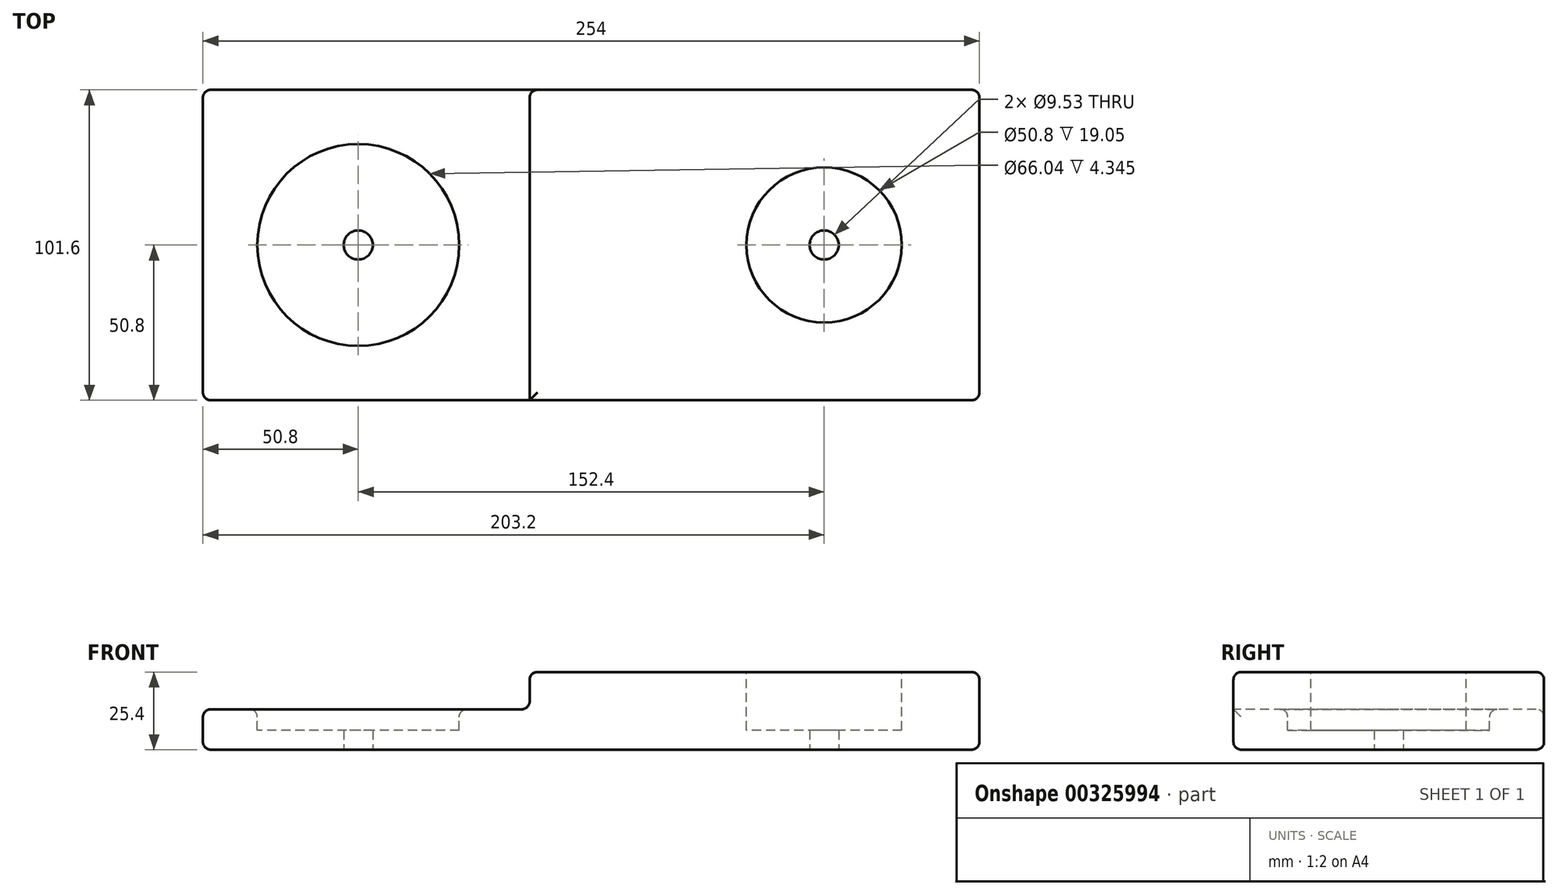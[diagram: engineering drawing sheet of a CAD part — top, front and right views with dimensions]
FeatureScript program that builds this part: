
annotation { "Feature Type Name" : "Feature", "Feature Type Description" : "" }
export const myFeature = defineFeature(function(context is Context, id is Id, definition is map)
    precondition{}
    {
        {
            var Q0;
            Q0=qCreatedBy(makeId("Top.planeOp"),FACE);
            var sketch = newSketch(context, id + "F0", { "sketchPlane" : qUnion([Q0])});
            skLineSegment(sketch, "E0", {"start": v(-127, -50.8) * mm, "end": v(127, -50.8) * mm});
            skLineSegment(sketch, "E1", {"start": v(127, -50.8) * mm, "end": v(127, 50.8) * mm});
            skLineSegment(sketch, "E2", {"start": v(127, 50.8) * mm, "end": v(-127, 50.8) * mm});
            skLineSegment(sketch, "E3", {"start": v(-127, 50.8) * mm, "end": v(-127, -50.8) * mm});
            skCircle(sketch, "E4", {"center": v(-76.2, 0) * mm, "radius": 4.76 * mm});
            skCircle(sketch, "E5", {"center": v(76.2, 0) * mm, "radius": 4.76 * mm});
            skSolve(sketch);
        }
        {
            var Q0;
            Q0=makeQuery(id+"F0.imprint","IMPRINT",FACE,{"disambiguationData":[TD([[makeQuery(id+"F0.imprint","IMPRINT",EDGE,{"derivedFrom":sQuery(id+"F0.wireOp",EDGE,"E0")}),1.0]])]});
            extrude(context, id + "F1", {"entities" : qUnion([Q0]), "depth" : 25.4 * mm});
        }
        {
            var Q0;
            Q0=makeQuery(id+"F1.opExtrude","CAP_FACE",FACE,{"disambiguationData":[OSD([sQuery(id+"F0.wireOp",EDGE,"E0"),sQuery(id+"F0.wireOp",EDGE,"E1"),sQuery(id+"F0.wireOp",EDGE,"E2"),sQuery(id+"F0.wireOp",EDGE,"E3"),sQuery(id+"F0.wireOp",EDGE,"E4"),sQuery(id+"F0.wireOp",EDGE,"E5")])],"isStart":false});
            var sketch = newSketch(context, id + "F2", { "sketchPlane" : qUnion([Q0])});
            skCircle(sketch, "E6", {"center": v(-76.2, 0) * mm, "radius": 33.02 * mm});
            skCircle(sketch, "E7", {"center": v(76.2, 0) * mm, "radius": 25.4 * mm});
            skSolve(sketch);
        }
        {
            var Q0;
            Q0=makeQuery(id+"F2.imprint","IMPRINT",FACE,{"disambiguationData":[TD([[makeQuery(id+"F2.imprint","IMPRINT",EDGE,{"derivedFrom":sQuery(id+"F2.wireOp",EDGE,"E6")}),1.0]])]});
            var Q1;
            Q1=makeQuery(id+"F2.imprint","IMPRINT",FACE,{"disambiguationData":[TD([[makeQuery(id+"F2.imprint","IMPRINT",EDGE,{"derivedFrom":sQuery(id+"F2.wireOp",EDGE,"E7")}),1.0]])]});
            extrude(context, id + "F3", {"entities" : qUnion([Q0, Q1]), "operationType" : NewBodyOperationType.REMOVE, "oppositeDirection" : true, "depth" : 19.05 * mm});
        }
        {
            var Q0;
            Q0=makeQuery(id+"F1.opExtrude","SWEPT_FACE",FACE,{"disambiguationData":[OSD([sQuery(id+"F0.wireOp",EDGE,"E0")])]});
            var sketch = newSketch(context, id + "F4", { "sketchPlane" : qUnion([Q0])});
            skLineSegment(sketch, "E8", {"start": v(-157.31, 13.23) * mm, "end": v(-20.15, 13.23) * mm});
            skLineSegment(sketch, "E9", {"start": v(-20.15, 13.23) * mm, "end": v(-20.15, 66.17) * mm});
            skLineSegment(sketch, "E10", {"start": v(-20.15, 66.17) * mm, "end": v(-138.96, 56.25) * mm});
            skLineSegment(sketch, "E11", {"start": v(-138.96, 56.25) * mm, "end": v(-157.31, 13.23) * mm});
            skSolve(sketch);
        }
        {
            var Q0;
            {var subQ0=sQuery(id+"F4.wireOp",EDGE,"E10");Q0=makeQuery(id+"F4.imprint","IMPRINT",FACE,{"disambiguationData":[TD([[makeQuery(id+"F4.imprint","IMPRINT",EDGE,{"derivedFrom":subQ0}),1.0]])]});}
            var Q1;
            {var subQ0=sQuery(id+"F4.wireOp",EDGE,"E9");var subQ1=sQuery(id+"F4.wireOp",EDGE,"E8");var subQ2=makeQuery(id+"F4.imprint","INTERSECT",VERTEX,{"derivedFrom":[subQ1,subQ0]});Q1=makeQuery(id+"F4.imprint","IMPRINT",FACE,{"disambiguationData":[TD([[makeQuery(id+"F4.imprint","IMPRINT",EDGE,{"disambiguationData":[TD([[subQ2,-1.0]])],"derivedFrom":subQ0}),1.0]])]});}
            extrude(context, id + "F5", {"entities" : qUnion([Q0, Q1]), "operationType" : NewBodyOperationType.REMOVE, "endBound" : BoundingType.THROUGH_ALL, "oppositeDirection" : true, "depth" : 25.4 * mm});
        }
        {
            var Q0;
            Q0=makeQuery(id+"F5.boolean.opBoolean","COPY",EDGE,{"derivedFrom":makeQuery(id+"F5.opExtrude","CAP_EDGE",EDGE,{"disambiguationData":[OSD([sQuery(id+"F4.wireOp",EDGE,"E8")])],"isStart":true})});
            var Q1;
            Q1=makeQuery(id+"F1.opExtrude","CAP_EDGE",EDGE,{"disambiguationData":[OSD([sQuery(id+"F0.wireOp",EDGE,"E0")])],"isStart":false});
            var Q2;
            Q2=makeQuery(id+"F5.boolean.opBoolean","COPY",EDGE,{"derivedFrom":makeQuery(id+"F5.opExtrude","CAP_EDGE",EDGE,{"disambiguationData":[OSD([sQuery(id+"F4.wireOp",EDGE,"E9")])],"isStart":true})});
            var Q3;
            Q3=makeQuery(id+"F1.opExtrude","SWEPT_EDGE",EDGE,{"disambiguationData":[OSD([sQuery(id+"F0.wireOp",EDGE,"E0"),sQuery(id+"F0.wireOp",EDGE,"E1")])]});
            var Q4;
            Q4=makeQuery(id+"F1.opExtrude","CAP_EDGE",EDGE,{"disambiguationData":[OSD([sQuery(id+"F0.wireOp",EDGE,"E0")])],"isStart":true});
            var Q5;
            Q5=makeQuery(id+"F1.opExtrude","CAP_EDGE",EDGE,{"disambiguationData":[OSD([sQuery(id+"F0.wireOp",EDGE,"E1")])],"isStart":false});
            var Q6;
            Q6=makeQuery(id+"F1.opExtrude","SWEPT_FACE",FACE,{"disambiguationData":[OSD([sQuery(id+"F0.wireOp",EDGE,"E1")])]});
            var Q7;
            Q7=makeQuery(id+"F1.opExtrude","CAP_EDGE",EDGE,{"disambiguationData":[OSD([sQuery(id+"F0.wireOp",EDGE,"E2")])],"isStart":false});
            var Q8;
            Q8=makeQuery(id+"F5.boolean.opBoolean","INTERSECT",EDGE,{"derivedFrom":[makeQuery(id+"F1.opExtrude","CAP_FACE",FACE,{"disambiguationData":[OSD([sQuery(id+"F0.wireOp",EDGE,"E0"),sQuery(id+"F0.wireOp",EDGE,"E1"),sQuery(id+"F0.wireOp",EDGE,"E2"),sQuery(id+"F0.wireOp",EDGE,"E3"),sQuery(id+"F0.wireOp",EDGE,"E4"),sQuery(id+"F0.wireOp",EDGE,"E5")])],"isStart":false}),makeQuery(id+"F5.opExtrude","SWEPT_FACE",FACE,{"disambiguationData":[OSD([sQuery(id+"F4.wireOp",EDGE,"E9")])]})]});
            var Q9;
            Q9=makeQuery(id+"F3.boolean.opBoolean","COPY",EDGE,{"derivedFrom":makeQuery(id+"F3.opExtrude","CAP_EDGE",EDGE,{"disambiguationData":[OSD([sQuery(id+"F2.wireOp",EDGE,"E7")])],"isStart":true})});
            var Q10;
            Q10=makeQuery(id+"F5.boolean.opBoolean","INTERSECT",EDGE,{"derivedFrom":[makeQuery(id+"F3.boolean.opBoolean","COPY",FACE,{"derivedFrom":makeQuery(id+"F3.opExtrude","SWEPT_FACE",FACE,{"disambiguationData":[OSD([sQuery(id+"F2.wireOp",EDGE,"E6")])]})}),makeQuery(id+"F5.opExtrude","SWEPT_FACE",FACE,{"disambiguationData":[OSD([sQuery(id+"F4.wireOp",EDGE,"E8")])]})]});
            var Q11;
            Q11=makeQuery(id+"F5.boolean.opBoolean","INTERSECT",EDGE,{"derivedFrom":[makeQuery(id+"F1.opExtrude","SWEPT_FACE",FACE,{"disambiguationData":[OSD([sQuery(id+"F0.wireOp",EDGE,"E2")])]}),makeQuery(id+"F5.opExtrude","SWEPT_FACE",FACE,{"disambiguationData":[OSD([sQuery(id+"F4.wireOp",EDGE,"E9")])]})]});
            var Q12;
            Q12=makeQuery(id+"F5.boolean.opBoolean","INTERSECT",EDGE,{"derivedFrom":[makeQuery(id+"F1.opExtrude","SWEPT_FACE",FACE,{"disambiguationData":[OSD([sQuery(id+"F0.wireOp",EDGE,"E2")])]}),makeQuery(id+"F5.opExtrude","SWEPT_FACE",FACE,{"disambiguationData":[OSD([sQuery(id+"F4.wireOp",EDGE,"E8")])]})]});
            var Q13;
            Q13=makeQuery(id+"F1.opExtrude","CAP_EDGE",EDGE,{"disambiguationData":[OSD([sQuery(id+"F0.wireOp",EDGE,"E2")])],"isStart":true});
            var Q14;
            Q14=makeQuery(id+"F1.opExtrude","CAP_EDGE",EDGE,{"disambiguationData":[OSD([sQuery(id+"F0.wireOp",EDGE,"E3")])],"isStart":true});
            var Q15;
            Q15=makeQuery(id+"F1.opExtrude","SWEPT_FACE",FACE,{"disambiguationData":[OSD([sQuery(id+"F0.wireOp",EDGE,"E3")])]});
            var Q16;
            Q16=makeQuery(id+"F5.boolean.opBoolean","COPY",EDGE,{"derivedFrom":makeQuery(id+"F5.opExtrude","SWEPT_EDGE",EDGE,{"disambiguationData":[OSD([sQuery(id+"F4.wireOp",EDGE,"E8"),sQuery(id+"F4.wireOp",EDGE,"E9")])]})});
            fillet(context, id + "F6", {"entities" : qUnion([Q0, Q1, Q2, Q3, Q4, Q5, Q6, Q7, Q8, Q9, Q10, Q11, Q12, Q13, Q14, Q15, Q16]), "radius" : 2.54 * mm, "tangentPropagation" : true, "allowEdgeOverflow" : false});
        }
    });
